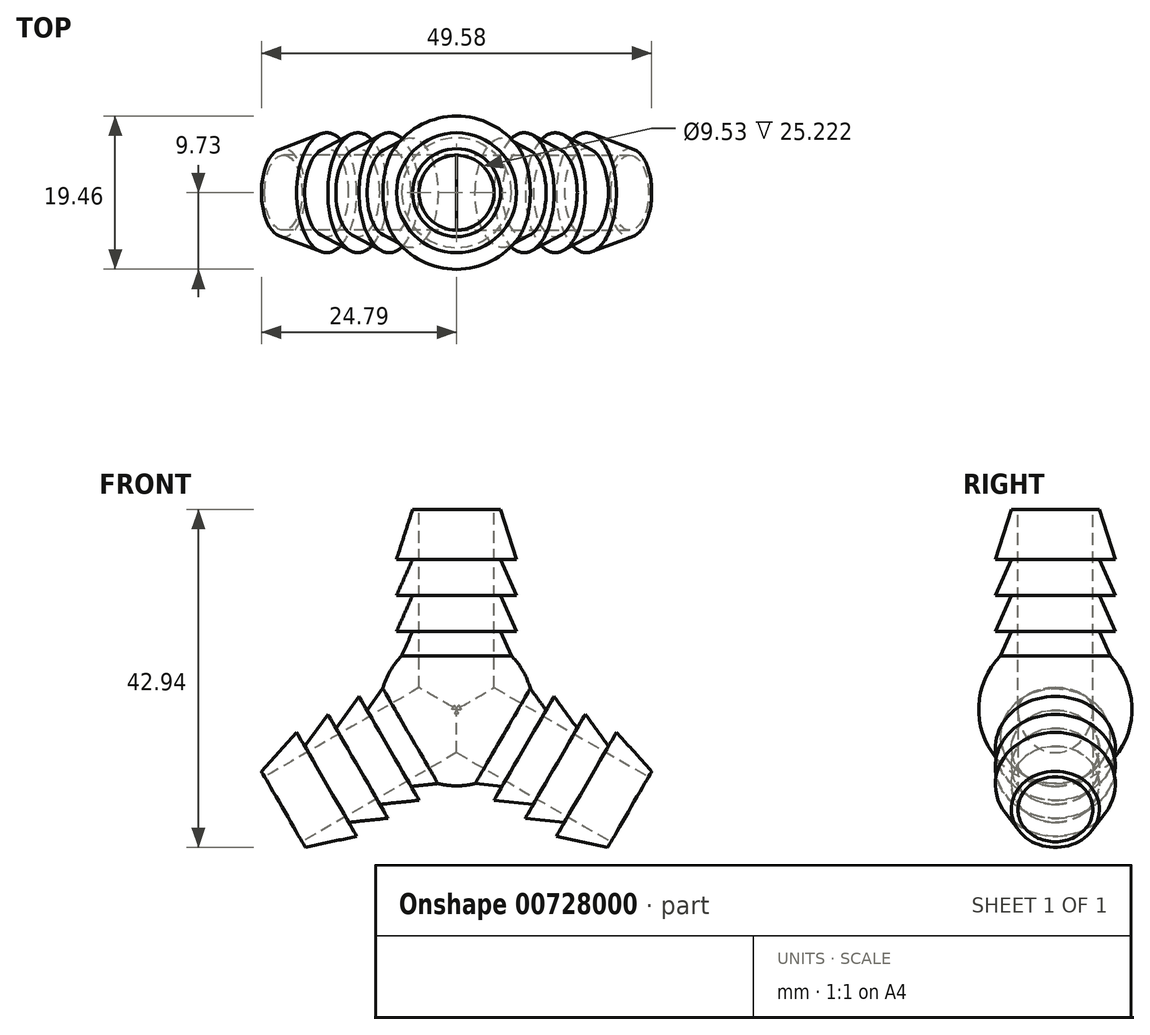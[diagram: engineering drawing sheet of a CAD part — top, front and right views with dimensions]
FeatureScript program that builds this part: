
annotation { "Feature Type Name" : "Feature", "Feature Type Description" : "" }
export const myFeature = defineFeature(function(context is Context, id is Id, definition is map)
    precondition{}
    {
        {
            var Q0;
            Q0=qCreatedBy(makeId("Front.planeOp"),FACE);
            var sketch = newSketch(context, id + "F0", { "sketchPlane" : qUnion([Q0])});
            skLineSegment(sketch, "E0", {"start": v(7.62, 25.4) * mm, "end": v(7.62, 25.4) * mm});
            skLineSegment(sketch, "E1", {"start": v(0, 25.4) * mm, "end": v(0, 50.8) * mm});
            skLineSegment(sketch, "E2", {"start": v(0, 50.8) * mm, "end": v(5.59, 50.8) * mm});
            skLineSegment(sketch, "E3", {"start": v(5.59, 25.4) * mm, "end": v(5.59, 50.8) * mm, "construction": true});
            skLineSegment(sketch, "E4", {"start": v(5.59, 50.8) * mm, "end": v(7.62, 44.45) * mm});
            skLineSegment(sketch, "E5", {"start": v(7.62, 44.45) * mm, "end": v(5.59, 44.45) * mm});
            skLineSegment(sketch, "E6", {"start": v(5.59, 44.45) * mm, "end": v(7.62, 39.88) * mm});
            skLineSegment(sketch, "E7", {"start": v(7.62, 39.88) * mm, "end": v(5.59, 39.88) * mm});
            skLineSegment(sketch, "E8", {"start": v(5.59, 39.88) * mm, "end": v(7.62, 35.3) * mm});
            skLineSegment(sketch, "E9", {"start": v(7.62, 35.3) * mm, "end": v(5.59, 35.3) * mm});
            skLineSegment(sketch, "E10", {"start": v(5.59, 35.3) * mm, "end": v(7.62, 30.73) * mm});
            skLineSegment(sketch, "E11", {"start": v(6.6, 25.4) * mm, "end": v(6.6, 25.4) * mm});
            skLineSegment(sketch, "E12.trimOffspring", {"start": v(7.62, 30.73) * mm, "end": v(7.62, 26.98) * mm});
            skPoint(sketch, "E13.orphan", {"position": v(7.62, 50.8) * mm});
            skLineSegment(sketch, "E14", {"start": v(7.62, 26.98) * mm, "end": v(7.62, 25.4) * mm});
            skLineSegment(sketch, "E15", {"start": v(7.62, 25.4) * mm, "end": v(0, 25.4) * mm});
            skLineSegment(sketch, "E16", {"start": v(-3.8, 32) * mm, "end": v(-3.8, 32) * mm});
            skLineSegment(sketch, "E17.trimOffspring", {"start": v(-3.8, 32) * mm, "end": v(-3.81, 32) * mm});
            skLineSegment(sketch, "E18", {"start": v(0, 25.4) * mm, "end": v(-22, 12.7) * mm});
            skLineSegment(sketch, "E19", {"start": v(-22, 12.7) * mm, "end": v(-24.8, 17.54) * mm});
            skLineSegment(sketch, "E20", {"start": v(-2.8, 30.24) * mm, "end": v(-24.8, 17.54) * mm, "construction": true});
            skLineSegment(sketch, "E21", {"start": v(-24.8, 17.54) * mm, "end": v(-20.3, 22.47) * mm});
            skLineSegment(sketch, "E22", {"start": v(-20.3, 22.47) * mm, "end": v(-19.3, 20.71) * mm});
            skLineSegment(sketch, "E23", {"start": v(-19.3, 20.71) * mm, "end": v(-16.35, 24.76) * mm});
            skLineSegment(sketch, "E24", {"start": v(-16.35, 24.76) * mm, "end": v(-15.33, 23) * mm});
            skLineSegment(sketch, "E25", {"start": v(-15.33, 23) * mm, "end": v(-12.39, 27.05) * mm});
            skLineSegment(sketch, "E26", {"start": v(-12.39, 27.05) * mm, "end": v(-11.37, 25.29) * mm});
            skLineSegment(sketch, "E27", {"start": v(-11.37, 25.29) * mm, "end": v(-8.43, 29.33) * mm});
            skLineSegment(sketch, "E28", {"start": v(-3.3, 31.12) * mm, "end": v(-3.3, 31.12) * mm});
            skLineSegment(sketch, "E29.trimOffspring", {"start": v(-8.43, 29.33) * mm, "end": v(-5.17, 31.21) * mm});
            skPoint(sketch, "E30.orphan", {"position": v(-25.8, 19.3) * mm});
            skLineSegment(sketch, "E31", {"start": v(-5.17, 31.21) * mm, "end": v(-3.8, 32) * mm});
            skLineSegment(sketch, "E32", {"start": v(-3.8, 32) * mm, "end": v(0, 25.4) * mm});
            skLineSegment(sketch, "E33.0", {"start": v(-20.3, 22.47) * mm, "end": v(-20.3, 22.47) * mm});
            skLineSegment(sketch, "E33.1", {"start": v(-20.3, 22.47) * mm, "end": v(-25.8, 19.3) * mm, "construction": true});
            skLineSegment(sketch, "E33.8", {"start": v(-16.35, 24.76) * mm, "end": v(-16.35, 24.76) * mm});
            skLineSegment(sketch, "E33.9", {"start": v(-16.35, 24.76) * mm, "end": v(-20.3, 22.47) * mm, "construction": true});
            skLineSegment(sketch, "E33.16", {"start": v(-12.39, 27.05) * mm, "end": v(-12.39, 27.05) * mm});
            skLineSegment(sketch, "E33.17", {"start": v(-12.39, 27.05) * mm, "end": v(-16.35, 24.76) * mm, "construction": true});
            skLineSegment(sketch, "E33.24", {"start": v(-8.43, 29.33) * mm, "end": v(-8.43, 29.33) * mm});
            skLineSegment(sketch, "E33.25", {"start": v(-8.43, 29.33) * mm, "end": v(-12.39, 27.05) * mm, "construction": true});
            skLineSegment(sketch, "E33.32", {"start": v(0, 25.4) * mm, "end": v(-2.8, 30.24) * mm, "construction": true});
            skLineSegment(sketch, "E33.33", {"start": v(0, 25.4) * mm, "end": v(0, 25.4) * mm});
            skLineSegment(sketch, "E34.0", {"start": v(-3.81, 32) * mm, "end": v(-25.8, 19.3) * mm, "construction": true});
            skLineSegment(sketch, "E35", {"start": v(-3.8, 18.8) * mm, "end": v(-3.82, 18.8) * mm});
            skLineSegment(sketch, "E36.trimOffspring", {"start": v(-3.82, 18.8) * mm, "end": v(-3.8, 18.8) * mm});
            skLineSegment(sketch, "E37", {"start": v(0, 25.4) * mm, "end": v(22, 12.7) * mm});
            skLineSegment(sketch, "E38", {"start": v(22, 12.7) * mm, "end": v(19.2, 7.86) * mm});
            skLineSegment(sketch, "E39", {"start": v(-2.8, 20.56) * mm, "end": v(19.2, 7.86) * mm, "construction": true});
            skLineSegment(sketch, "E40", {"start": v(19.2, 7.86) * mm, "end": v(12.69, 9.28) * mm});
            skLineSegment(sketch, "E41", {"start": v(12.69, 9.28) * mm, "end": v(13.7, 11.04) * mm});
            skLineSegment(sketch, "E42", {"start": v(13.7, 11.04) * mm, "end": v(8.73, 11.56) * mm});
            skLineSegment(sketch, "E43", {"start": v(8.73, 11.56) * mm, "end": v(9.74, 13.32) * mm});
            skLineSegment(sketch, "E44", {"start": v(9.74, 13.32) * mm, "end": v(4.77, 13.85) * mm});
            skLineSegment(sketch, "E45", {"start": v(4.77, 13.85) * mm, "end": v(5.78, 15.6) * mm});
            skLineSegment(sketch, "E46", {"start": v(5.78, 15.6) * mm, "end": v(0.8, 16.13) * mm});
            skLineSegment(sketch, "E47", {"start": v(-3.3, 19.68) * mm, "end": v(-3.3, 19.68) * mm});
            skLineSegment(sketch, "E48.trimOffspring", {"start": v(0.8, 16.13) * mm, "end": v(-2.45, 18.01) * mm});
            skPoint(sketch, "E49.orphan", {"position": v(18.19, 6.1) * mm});
            skLineSegment(sketch, "E50", {"start": v(-2.45, 18.01) * mm, "end": v(-3.8, 18.8) * mm});
            skLineSegment(sketch, "E51", {"start": v(-3.8, 18.8) * mm, "end": v(0, 25.4) * mm});
            skLineSegment(sketch, "E52.0", {"start": v(12.69, 9.28) * mm, "end": v(12.69, 9.28) * mm});
            skLineSegment(sketch, "E52.1", {"start": v(12.69, 9.28) * mm, "end": v(18.19, 6.1) * mm, "construction": true});
            skLineSegment(sketch, "E52.8", {"start": v(8.73, 11.56) * mm, "end": v(8.73, 11.56) * mm});
            skLineSegment(sketch, "E52.9", {"start": v(8.73, 11.56) * mm, "end": v(12.69, 9.28) * mm, "construction": true});
            skLineSegment(sketch, "E52.16", {"start": v(4.77, 13.85) * mm, "end": v(4.77, 13.85) * mm});
            skLineSegment(sketch, "E52.17", {"start": v(4.77, 13.85) * mm, "end": v(8.73, 11.56) * mm, "construction": true});
            skLineSegment(sketch, "E52.24", {"start": v(0.8, 16.13) * mm, "end": v(0.8, 16.13) * mm});
            skLineSegment(sketch, "E52.25", {"start": v(0.8, 16.13) * mm, "end": v(4.77, 13.85) * mm, "construction": true});
            skLineSegment(sketch, "E52.32", {"start": v(0, 25.4) * mm, "end": v(-2.8, 20.56) * mm, "construction": true});
            skLineSegment(sketch, "E53.0", {"start": v(-3.8, 18.8) * mm, "end": v(18.19, 6.1) * mm, "construction": true});
            skSolve(sketch);
        }
        {
            var Q0;
            {var subQ1=sQuery(id+"F0.wireOp",EDGE,"E2");Q0=makeQuery(id+"F0.imprint","IMPRINT",FACE,{"disambiguationData":[TD([[makeQuery(id+"F0.imprint","IMPRINT",EDGE,{"derivedFrom":subQ1}),-1.0]])]});}
            var Q1;
            Q1=sQuery(id+"F0.wireOp",EDGE,"E1");
            revolve(context, id + "F1", {"entities" : qUnion([Q0]), "axis" : qUnion([Q1]), "revolveType" : RevolveType.FULL, "surfaceOperationType" : NewSurfaceOperationType.NEW});
        }
        {
            var Q0;
            {var subQ1=sQuery(id+"F0.wireOp",EDGE,"E18");Q0=makeQuery(id+"F0.imprint","IMPRINT",FACE,{"disambiguationData":[TD([[makeQuery(id+"F0.imprint","IMPRINT",EDGE,{"derivedFrom":subQ1}),-1.0]])]});}
            var Q1;
            {var subQ4=sQuery(id+"F0.wireOp",EDGE,"E19");Q1=makeQuery(id+"F0.imprint","IMPRINT",FACE,{"disambiguationData":[TD([[makeQuery(id+"F0.imprint","IMPRINT",EDGE,{"derivedFrom":subQ4}),-1.0]])]});}
            var Q2;
            Q2=sQuery(id+"F0.wireOp",EDGE,"E18");
            revolve(context, id + "F2", {"operationType" : NewBodyOperationType.ADD, "surfaceOperationType" : NewSurfaceOperationType.NEW, "entities" : qUnion([Q0, Q1]), "axis" : qUnion([Q2]), "revolveType" : RevolveType.FULL});
        }
        {
            var Q0;
            {var subQ1=sQuery(id+"F0.wireOp",EDGE,"E38");Q0=makeQuery(id+"F0.imprint","IMPRINT",FACE,{"disambiguationData":[TD([[makeQuery(id+"F0.imprint","IMPRINT",EDGE,{"derivedFrom":subQ1}),-1.0]])]});}
            var Q1;
            Q1=sQuery(id+"F0.wireOp",EDGE,"E37");
            revolve(context, id + "F3", {"operationType" : NewBodyOperationType.ADD, "surfaceOperationType" : NewSurfaceOperationType.NEW, "entities" : qUnion([Q0]), "axis" : qUnion([Q1]), "revolveType" : RevolveType.FULL});
        }
        {
            var Q0;
            Q0=qCreatedBy(makeId("Front.planeOp"),FACE);
            var sketch = newSketch(context, id + "F4", { "sketchPlane" : qUnion([Q0])});
            skLineSegment(sketch, "E54", {"start": v(0, 25.4) * mm, "end": v(0, 0) * mm});
            skArc(sketch, "E55", {"start": v(0, 35.14) * mm, "mid": v(-9.73, 25.4) * mm, "end": v(0, 15.68) * mm});
            skLineSegment(sketch, "E56", {"start": v(0, 35.14) * mm, "end": v(0, 15.68) * mm});
            skSolve(sketch);
        }
        {
            var Q0;
            {var subQ0=sQuery(id+"F4.wireOp",EDGE,"E55");Q0=makeQuery(id+"F4.imprint","IMPRINT",FACE,{"disambiguationData":[TD([[makeQuery(id+"F4.imprint","IMPRINT",EDGE,{"derivedFrom":subQ0}),1.0]])]});}
            var Q1;
            Q1=sQuery(id+"F4.wireOp",EDGE,"E56");
            revolve(context, id + "F5", {"operationType" : NewBodyOperationType.ADD, "surfaceOperationType" : NewSurfaceOperationType.NEW, "entities" : qUnion([Q0]), "axis" : qUnion([Q1]), "revolveType" : RevolveType.FULL});
        }
        {
            var Q0;
            Q0=makeQuery(id+"F1.opRevolve","SWEPT_FACE",FACE,{"disambiguationData":[OSD([sQuery(id+"F0.wireOp",EDGE,"E2")])]});
            var sketch = newSketch(context, id + "F6", { "sketchPlane" : qUnion([Q0])});
            skCircle(sketch, "E57", {"center": v(0, 0) * mm, "radius": 4.76 * mm});
            skSolve(sketch);
        }
        {
            var Q0;
            Q0=makeQuery(id+"F3.opRevolve","SWEPT_FACE",FACE,{"disambiguationData":[OSD([sQuery(id+"F0.wireOp",EDGE,"E38")])]});
            var sketch = newSketch(context, id + "F7", { "sketchPlane" : qUnion([Q0])});
            skCircle(sketch, "E58", {"center": v(0, 22) * mm, "radius": 4.77 * mm});
            skSolve(sketch);
        }
        {
            var Q0;
            Q0=makeQuery(id+"F2.opRevolve","SWEPT_FACE",FACE,{"disambiguationData":[OSD([sQuery(id+"F0.wireOp",EDGE,"E19")])]});
            var sketch = newSketch(context, id + "F8", { "sketchPlane" : qUnion([Q0])});
            skCircle(sketch, "E59", {"center": v(0, 22) * mm, "radius": 4.77 * mm});
            skSolve(sketch);
        }
        {
            var Q0;
            Q0=makeQuery(id+"F6.imprint","IMPRINT",FACE,{"disambiguationData":[TD([[makeQuery(id+"F6.imprint","IMPRINT",EDGE,{"derivedFrom":sQuery(id+"F6.wireOp",EDGE,"E57")}),1.0]])]});
            var Q2;
            Q2=sQuery(id+"F4.wireOp",VERTEX,"E55.center");
            extrude(context, id + "F9", {"entities" : qUnion([Q0]), "operationType" : NewBodyOperationType.REMOVE, "endBound" : BoundingType.UP_TO_VERTEX, "oppositeDirection" : true, "depth" : 25.4 * mm, "endBoundEntityVertex" : qUnion([Q2]), "hasOffset" : true, "offsetDistance" : 0.5 * mm, "offsetOppositeDirection" : true});
        }
        {
            var Q0;
            Q0=makeQuery(id+"F7.imprint","IMPRINT",FACE,{"disambiguationData":[TD([[makeQuery(id+"F7.imprint","IMPRINT",EDGE,{"derivedFrom":sQuery(id+"F7.wireOp",EDGE,"E58")}),1.0]])]});
            var Q1;
            Q1=sQuery(id+"F0.wireOp",VERTEX,"E33.32.start");
            extrude(context, id + "F10", {"entities" : qUnion([Q0]), "operationType" : NewBodyOperationType.REMOVE, "endBound" : BoundingType.UP_TO_VERTEX, "oppositeDirection" : true, "depth" : 25 * mm, "endBoundEntityVertex" : qUnion([Q1]), "hasOffset" : true, "offsetDistance" : .5 * mm, "offsetOppositeDirection" : true});
        }
        {
            var Q0;
            Q0=makeQuery(id+"F8.imprint","IMPRINT",FACE,{"disambiguationData":[TD([[makeQuery(id+"F8.imprint","IMPRINT",EDGE,{"derivedFrom":sQuery(id+"F8.wireOp",EDGE,"E59")}),1.0]])]});
            var Q1;
            Q1=sQuery(id+"F4.wireOp",VERTEX,"E55.center");
            extrude(context, id + "F11", {"entities" : qUnion([Q0]), "operationType" : NewBodyOperationType.REMOVE, "endBound" : BoundingType.UP_TO_VERTEX, "oppositeDirection" : true, "depth" : 25 * mm, "endBoundEntityVertex" : qUnion([Q1]), "hasOffset" : true, "offsetDistance" : .5 * mm, "offsetOppositeDirection" : true});
        }
    });
